# Revit family: 315L Cylinder
name_source: partatom
category: Generic Models
revit_build: Autodesk Revit 2018 (Build: 20170223_1515(x64)
units: mm (PartAtom-declared; Revit-internal decimal feet)

## family parameters
Can host rebar = No
Cut with Voids When Loaded = No
Host = Face
Part Type = Normal
Room Calculation Point = No
Round Connector Dimension = Use Diameter
Shared = No

## types (1)
- 315L Cylinder
    Angle (Hot & Cold) = 0.00°
    Angle (TPR 1) = 22.00°
    Angle (TPR 2) = 43.00°
    Angle (Thermowell Port) = 90.00°
    Cold Inlet Connection = DN32
    Cold Inlet/ Thermowell Height = 285 mm  [stored 0.935039 ft]
    Connection Radii = 300 mm  [stored 0.984252 ft]
    Cylinder Height = 2083 mm
    Default Elevation = 1219 mm
    Description = Demand Duo 315L Storage Cylinder
    Hot Outlet Connection = DN32
    Hot Outlet Height = 1855 mm  [stored 6.08596 ft]
    Hot Return Connection = DN32
    Hot Return Height = 385 mm
    Installation = In accordance with G12 and AS/NZS 3500.4
    Manufacturer = Rinnai
    Model = BE18002776
    Seismic Restraint = In accordance with G12/AS1 Figure 14
    TPR Connection = DN20
    TPR Valve (Supplied) = 850kPa, 99 °C, 46 kW
    Thermowell Connection = DN20
    URL = https://rinnai.co.nz
    Warranty (Labour) = 1 Year
    Warranty (Parts) = 5 Years
    Weights - empty/full = 61kg / 381kg

note: [stored X ft] marks values corroborated as IEEE doubles in the binary element streams (Revit-internal decimal feet)

## geometry (parser evidence)
native form markers: Sweep x2
no freeform markers — native parametric forms only
